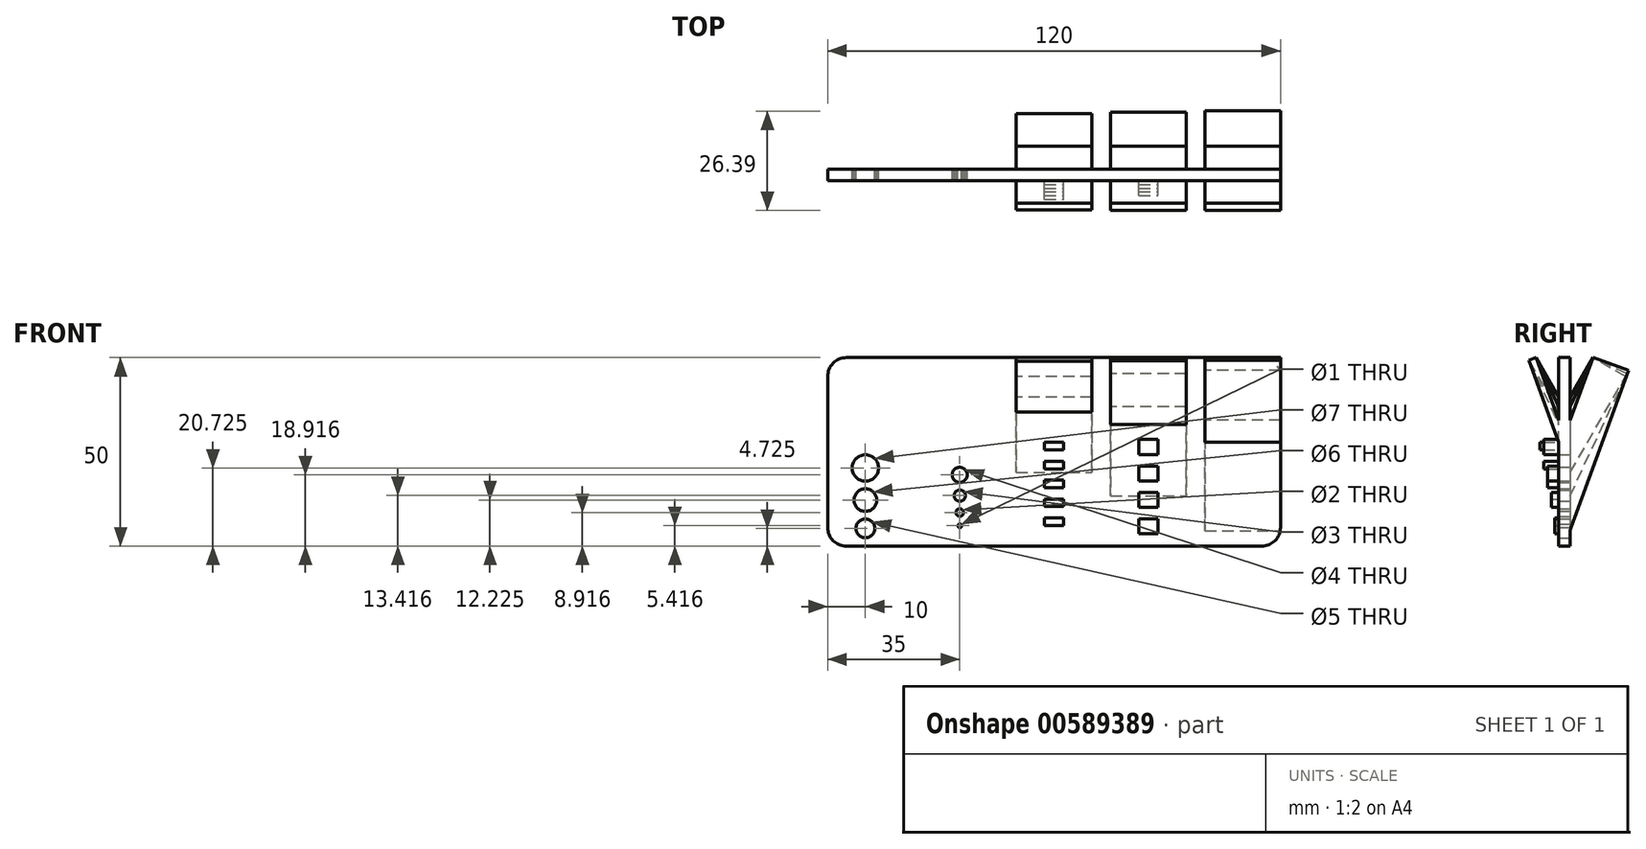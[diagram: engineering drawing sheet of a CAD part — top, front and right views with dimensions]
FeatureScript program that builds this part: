
annotation { "Feature Type Name" : "Feature", "Feature Type Description" : "" }
export const myFeature = defineFeature(function(context is Context, id is Id, definition is map)
    precondition{}
    {
        {
            var Q0;
            Q0=qCreatedBy(makeId("Top.planeOp"),FACE);
            var sketch = newSketch(context, id + "F0", { "sketchPlane" : qUnion([Q0])});
            skLineSegment(sketch, "E0", {"start": v(-60, 1.5) * mm, "end": v(-1.5, 1.5) * mm});
            skLineSegment(sketch, "E1", {"start": v(-1.5, 1.5) * mm, "end": v(-1.5, 15) * mm});
            skLineSegment(sketch, "E2", {"start": v(-1.5, 15) * mm, "end": v(1.5, 15) * mm});
            skLineSegment(sketch, "E3", {"start": v(1.5, 15) * mm, "end": v(1.5, 1.5) * mm});
            skLineSegment(sketch, "E4", {"start": v(1.5, 1.5) * mm, "end": v(60, 1.5) * mm});
            skLineSegment(sketch, "E5", {"start": v(60, 1.5) * mm, "end": v(60, -1.5) * mm});
            skLineSegment(sketch, "E6", {"start": v(60, -1.5) * mm, "end": v(1.5, -1.5) * mm});
            skLineSegment(sketch, "E7", {"start": v(1.5, -1.5) * mm, "end": v(1.5, -15) * mm});
            skLineSegment(sketch, "E8", {"start": v(1.5, -15) * mm, "end": v(-1.5, -15) * mm});
            skLineSegment(sketch, "E9", {"start": v(-1.5, -15) * mm, "end": v(-1.5, -1.5) * mm});
            skLineSegment(sketch, "E10", {"start": v(-1.5, -1.5) * mm, "end": v(-60, -1.5) * mm});
            skLineSegment(sketch, "E11", {"start": v(-60, -1.5) * mm, "end": v(-60, 1.5) * mm});
            skLineSegment(sketch, "E12", {"start": v(0, 15) * mm, "end": v(0, 0) * mm, "construction": true});
            skLineSegment(sketch, "E13", {"start": v(-60, 0) * mm, "end": v(0, 0) * mm});
            skLineSegment(sketch, "E14", {"start": v(-1.5, -1.5) * mm, "end": v(1.5, -1.5) * mm});
            skLineSegment(sketch, "E15", {"start": v(-1.5, 1.5) * mm, "end": v(1.5, 1.5) * mm});
            skLineSegment(sketch, "E16", {"start": v(1.5, 1.5) * mm, "end": v(1.5, -1.5) * mm});
            skLineSegment(sketch, "E17", {"start": v(-1.5, -1.5) * mm, "end": v(-1.5, 1.5) * mm});
            skSolve(sketch);
        }
        {
            var Q0;
            {var subQ0=sQuery(id+"F0.wireOp",EDGE,"E10");Q0=makeQuery(id+"F0.imprint","IMPRINT",FACE,{"disambiguationData":[TD([[makeQuery(id+"F0.imprint","IMPRINT",EDGE,{"derivedFrom":subQ0}),-1.0]])]});}
            var Q1;
            {var subQ0=sQuery(id+"F0.wireOp",EDGE,"E0");Q1=makeQuery(id+"F0.imprint","IMPRINT",FACE,{"disambiguationData":[TD([[makeQuery(id+"F0.imprint","IMPRINT",EDGE,{"derivedFrom":subQ0}),-1.0]])]});}
            var Q2;
            {var subQ1=sQuery(id+"F0.wireOp",EDGE,"E14");Q2=makeQuery(id+"F0.imprint","IMPRINT",FACE,{"disambiguationData":[TD([[makeQuery(id+"F0.imprint","IMPRINT",EDGE,{"derivedFrom":subQ1}),1.0]])]});}
            var Q3;
            Q3=makeQuery(id+"F0.imprint","IMPRINT",FACE,{"disambiguationData":[TD([[makeQuery(id+"F0.imprint","IMPRINT",EDGE,{"derivedFrom":sQuery(id+"F0.wireOp",EDGE,"E4")}),-1.0]])]});
            extrude(context, id + "F1", {"entities" : qUnion([Q0, Q1, Q2, Q3]), "depth" : 50 * mm, "offsetDistance" : 25 * mm});
        }
        {
            var Q0;
            Q0=qCreatedBy(makeId("Right.planeOp"),FACE);
            cPlane(context, id + "F2", {"entities" : qUnion([Q0]), "cplaneType" : CPlaneType.OFFSET, "offset" : 25 * mm, "width" : 150 * mm, "height" : 150 * mm});
        }
        {
            var Q0;
            Q0=qCreatedBy(makeId("Right.planeOp"),FACE);
            cPlane(context, id + "F3", {"entities" : qUnion([Q0]), "cplaneType" : CPlaneType.OFFSET, "offset" : 50 * mm, "width" : 150 * mm, "height" : 150 * mm});
        }
        {
            var Q0;
            Q0=qCreatedBy(id+"F3.planeOp",FACE);
            var sketch = newSketch(context, id + "F4", { "sketchPlane" : qUnion([Q0])});
            skLineSegment(sketch, "E18", {"start": v(0, 0) * mm, "end": v(16.95, 46.58) * mm});
            skLineSegment(sketch, "E19", {"start": v(16.95, 46.58) * mm, "end": v(7.56, 50) * mm});
            skLineSegment(sketch, "E20", {"start": v(7.56, 50) * mm, "end": v(0, 29.24) * mm});
            skLineSegment(sketch, "E21", {"start": v(0, 29.24) * mm, "end": v(0, 0) * mm});
            skLineSegment(sketch, "E22", {"start": v(0, 29.24) * mm, "end": v(-7.56, 50) * mm});
            skLineSegment(sketch, "E23", {"start": v(-7.56, 50) * mm, "end": v(-9.44, 49.32) * mm});
            skLineSegment(sketch, "E24", {"start": v(-9.44, 49.32) * mm, "end": v(0, 23.4) * mm});
            skLineSegment(sketch, "E25", {"start": v(0, 23.4) * mm, "end": v(0, 29.24) * mm});
            skSolve(sketch);
        }
        {
            var Q0;
            Q0=qCreatedBy(id+"F2.planeOp",FACE);
            var sketch = newSketch(context, id + "F5", { "sketchPlane" : qUnion([Q0])});
            skLineSegment(sketch, "E26", {"start": v(0, 10.13) * mm, "end": v(16.62, 45.77) * mm});
            skLineSegment(sketch, "E27", {"start": v(16.62, 45.77) * mm, "end": v(7.56, 50) * mm});
            skLineSegment(sketch, "E28", {"start": v(7.56, 50) * mm, "end": v(0, 33.8) * mm});
            skLineSegment(sketch, "E29", {"start": v(0, 33.8) * mm, "end": v(0, 10.13) * mm});
            skLineSegment(sketch, "E30", {"start": v(0, 33.8) * mm, "end": v(-7.56, 50) * mm});
            skLineSegment(sketch, "E31", {"start": v(-7.56, 50) * mm, "end": v(-9.37, 49.15) * mm});
            skLineSegment(sketch, "E32", {"start": v(-9.37, 49.15) * mm, "end": v(0, 29.06) * mm});
            skLineSegment(sketch, "E33", {"start": v(0, 29.06) * mm, "end": v(0, 33.8) * mm});
            skSolve(sketch);
        }
        {
            var Q0;
            Q0=qCreatedBy(makeId("Right.planeOp"),FACE);
            var sketch = newSketch(context, id + "F6", { "sketchPlane" : qUnion([Q0])});
            skLineSegment(sketch, "E34", {"start": v(0, 16.91) * mm, "end": v(16.22, 45) * mm});
            skLineSegment(sketch, "E35", {"start": v(16.22, 45) * mm, "end": v(7.56, 50) * mm});
            skLineSegment(sketch, "E36", {"start": v(7.56, 50) * mm, "end": v(0, 36.91) * mm});
            skLineSegment(sketch, "E37", {"start": v(0, 36.91) * mm, "end": v(0, 16.91) * mm});
            skLineSegment(sketch, "E38", {"start": v(0, 36.91) * mm, "end": v(-7.56, 50) * mm});
            skLineSegment(sketch, "E39", {"start": v(-7.56, 50) * mm, "end": v(-9.29, 49) * mm});
            skLineSegment(sketch, "E40", {"start": v(-9.29, 49) * mm, "end": v(0, 32.91) * mm});
            skLineSegment(sketch, "E41", {"start": v(0, 32.91) * mm, "end": v(0, 36.91) * mm});
            skSolve(sketch);
        }
        {
            var Q0;
            Q0=qCreatedBy(id+"F3WGKMQ0B0yvw4O_1.1.F2.planeOp",FACE);
            var sketch = newSketch(context, id + "F7", { "sketchPlane" : qUnion([Q0])});
            skLineSegment(sketch, "E42", {"start": v(0, 21.77) * mm, "end": v(-15.75, 44.26) * mm});
            skLineSegment(sketch, "E43", {"start": v(-15.75, 44.26) * mm, "end": v(-7.56, 50) * mm});
            skLineSegment(sketch, "E44", {"start": v(-7.56, 50) * mm, "end": v(0, 39.2) * mm});
            skLineSegment(sketch, "E45", {"start": v(0, 39.2) * mm, "end": v(0, 21.77) * mm});
            skLineSegment(sketch, "E46", {"start": v(0, 39.2) * mm, "end": v(7.56, 50) * mm});
            skLineSegment(sketch, "E47", {"start": v(7.56, 50) * mm, "end": v(9.2, 48.85) * mm});
            skLineSegment(sketch, "E48", {"start": v(9.2, 48.85) * mm, "end": v(0, 35.72) * mm});
            skLineSegment(sketch, "E49", {"start": v(0, 35.72) * mm, "end": v(0, 39.2) * mm});
            skSolve(sketch);
        }
        {
            var Q0;
            Q0=qCreatedBy(id+"F3WGKMQ0B0yvw4O_1.1.F3.planeOp",FACE);
            var sketch = newSketch(context, id + "F8", { "sketchPlane" : qUnion([Q0])});
            skLineSegment(sketch, "E50", {"start": v(0, 25.44) * mm, "end": v(-15.22, 43.57) * mm});
            skLineSegment(sketch, "E51", {"start": v(-15.22, 43.57) * mm, "end": v(-7.56, 50) * mm});
            skLineSegment(sketch, "E52", {"start": v(-7.56, 50) * mm, "end": v(0, 41) * mm});
            skLineSegment(sketch, "E53", {"start": v(0, 41) * mm, "end": v(0, 25.44) * mm});
            skLineSegment(sketch, "E54", {"start": v(0, 41) * mm, "end": v(7.56, 50) * mm});
            skLineSegment(sketch, "E55", {"start": v(7.56, 50) * mm, "end": v(9.09, 48.71) * mm});
            skLineSegment(sketch, "E56", {"start": v(9.09, 48.71) * mm, "end": v(0, 37.88) * mm});
            skLineSegment(sketch, "E57", {"start": v(0, 37.88) * mm, "end": v(0, 41) * mm});
            skSolve(sketch);
        }
        {
            var Q0;
            Q0 = qSketchRegion(id + "F4", true);
            var Q1;
            Q1 = qSketchRegion(id + "F5", true);
            var Q2;
            Q2 = qSketchRegion(id + "F6", true);
            var Q3;
            Q3 = qSketchRegion(id + "F7", true);
            var Q4;
            Q4 = qSketchRegion(id + "F8", true);
            extrude(context, id + "F9", {"entities" : qUnion([Q0, Q1, Q2, Q3, Q4]), "operationType" : NewBodyOperationType.ADD, "endBound" : BoundingType.SYMMETRIC, "depth" : 20 * mm, "offsetDistance" : 25 * mm});
        }
        {
            var Q0;
            Q0=makeQuery(id+"F1.opExtrude","CAP_EDGE",EDGE,{"disambiguationData":[OSD([sQuery(id+"F0.wireOp",EDGE,"E11")])],"isStart":true});
            var Q1;
            Q1=makeQuery(id+"F1.opExtrude","CAP_EDGE",EDGE,{"disambiguationData":[OSD([sQuery(id+"F0.wireOp",EDGE,"E5")])],"isStart":false});
            var Q2;
            Q2=makeQuery(id+"F1.opExtrude","CAP_EDGE",EDGE,{"disambiguationData":[OSD([sQuery(id+"F0.wireOp",EDGE,"E5")])],"isStart":true});
            var Q3;
            Q3=makeQuery(id+"F1.opExtrude","CAP_EDGE",EDGE,{"disambiguationData":[OSD([sQuery(id+"F0.wireOp",EDGE,"E11")])],"isStart":false});
            fillet(context, id + "F10", {"entities" : qUnion([Q0, Q1, Q2, Q3]), "radius" : 5 * mm, "tangentPropagation" : true, "allowEdgeOverflow" : false});
        }
        {
            var Q0;
            Q0=makeQuery(id+"F1.opExtrude","SWEPT_FACE",FACE,{"disambiguationData":[OSD([sQuery(id+"F0.wireOp",EDGE,"E0"),sQuery(id+"F0.wireOp",EDGE,"E4"),sQuery(id+"F0.wireOp",EDGE,"E15")])]});
            var sketch = newSketch(context, id + "F11", { "sketchPlane" : qUnion([Q0])});
            skCircle(sketch, "E58", {"center": v(25, 5.42) * mm, "radius": 0.5 * mm});
            skCircle(sketch, "E59", {"center": v(25, 8.92) * mm, "radius": 1 * mm});
            skCircle(sketch, "E60", {"center": v(25, 13.42) * mm, "radius": 1.5 * mm});
            skCircle(sketch, "E61", {"center": v(25, 18.92) * mm, "radius": 2 * mm});
            skCircle(sketch, "E62", {"center": v(50, 4.72) * mm, "radius": 2.5 * mm});
            skCircle(sketch, "E63", {"center": v(50, 12.22) * mm, "radius": 3 * mm});
            skCircle(sketch, "E64", {"center": v(50, 20.72) * mm, "radius": 3.5 * mm});
            skSolve(sketch);
        }
        {
            var Q0;
            Q0 = qSketchRegion(id + "F11", true);
            extrude(context, id + "F12", {"entities" : qUnion([Q0]), "operationType" : NewBodyOperationType.REMOVE, "endBound" : BoundingType.UP_TO_NEXT, "oppositeDirection" : true, "depth" : 25 * mm, "offsetDistance" : 25 * mm});
        }
        {
            var Q0;
            Q0=makeQuery(id+"F1.opExtrude","SWEPT_FACE",FACE,{"disambiguationData":[OSD([sQuery(id+"F0.wireOp",EDGE,"E6"),sQuery(id+"F0.wireOp",EDGE,"E10"),sQuery(id+"F0.wireOp",EDGE,"E14")])]});
            var sketch = newSketch(context, id + "F13", { "sketchPlane" : qUnion([Q0])});
            skLineSegment(sketch, "E65.bottom", {"start": v(-2.5, 7.5) * mm, "end": v(2.5, 7.5) * mm});
            skLineSegment(sketch, "E65.top", {"start": v(-2.5, 5.5) * mm, "end": v(2.5, 5.5) * mm});
            skLineSegment(sketch, "E65.left", {"start": v(-2.5, 7.5) * mm, "end": v(-2.5, 5.5) * mm});
            skLineSegment(sketch, "E65.right", {"start": v(2.5, 7.5) * mm, "end": v(2.5, 5.5) * mm});
            skLineSegment(sketch, "E66.1.0.0", {"start": v(-2.5, 12.5) * mm, "end": v(2.5, 12.5) * mm});
            skLineSegment(sketch, "E66.1.0.1", {"start": v(2.5, 12.5) * mm, "end": v(2.5, 10.5) * mm});
            skLineSegment(sketch, "E66.1.0.2", {"start": v(-2.5, 10.5) * mm, "end": v(2.5, 10.5) * mm});
            skLineSegment(sketch, "E66.1.0.3", {"start": v(-2.5, 12.5) * mm, "end": v(-2.5, 10.5) * mm});
            skLineSegment(sketch, "E66.2.0.0", {"start": v(-2.5, 17.5) * mm, "end": v(2.5, 17.5) * mm});
            skLineSegment(sketch, "E66.2.0.1", {"start": v(2.5, 17.5) * mm, "end": v(2.5, 15.5) * mm});
            skLineSegment(sketch, "E66.2.0.2", {"start": v(-2.5, 15.5) * mm, "end": v(2.5, 15.5) * mm});
            skLineSegment(sketch, "E66.2.0.3", {"start": v(-2.5, 17.5) * mm, "end": v(-2.5, 15.5) * mm});
            skLineSegment(sketch, "E66.3.0.0", {"start": v(-2.5, 22.5) * mm, "end": v(2.5, 22.5) * mm});
            skLineSegment(sketch, "E66.3.0.1", {"start": v(2.5, 22.5) * mm, "end": v(2.5, 20.5) * mm});
            skLineSegment(sketch, "E66.3.0.2", {"start": v(-2.5, 20.5) * mm, "end": v(2.5, 20.5) * mm});
            skLineSegment(sketch, "E66.3.0.3", {"start": v(-2.5, 22.5) * mm, "end": v(-2.5, 20.5) * mm});
            skLineSegment(sketch, "E66.4.0.0", {"start": v(-2.5, 27.5) * mm, "end": v(2.5, 27.5) * mm});
            skLineSegment(sketch, "E66.4.0.1", {"start": v(2.5, 27.5) * mm, "end": v(2.5, 25.5) * mm});
            skLineSegment(sketch, "E66.4.0.2", {"start": v(-2.5, 25.5) * mm, "end": v(2.5, 25.5) * mm});
            skLineSegment(sketch, "E66.4.0.3", {"start": v(-2.5, 27.5) * mm, "end": v(-2.5, 25.5) * mm});
            skLineSegment(sketch, "E66.direction1", {"start": v(-2.5, 7.5) * mm, "end": v(-2.5, 12.5) * mm, "construction": true});
            skSolve(sketch);
        }
        {
            var Q0;
            Q0=makeQuery(id+"F13.imprint","IMPRINT",FACE,{"disambiguationData":[TD([[makeQuery(id+"F13.imprint","IMPRINT",EDGE,{"derivedFrom":sQuery(id+"F13.wireOp",EDGE,"E65.bottom")}),1.0]])]});
            var sketch = newSketch(context, id + "F14", { "sketchPlane" : qUnion([Q0])});
            skLineSegment(sketch, "E67.bottom", {"start": v(22.5, 7.28) * mm, "end": v(27.5, 7.28) * mm});
            skLineSegment(sketch, "E67.top", {"start": v(22.5, 3.28) * mm, "end": v(27.5, 3.28) * mm});
            skLineSegment(sketch, "E67.left", {"start": v(22.5, 7.28) * mm, "end": v(22.5, 3.28) * mm});
            skLineSegment(sketch, "E67.right", {"start": v(27.5, 7.28) * mm, "end": v(27.5, 3.28) * mm});
            skLineSegment(sketch, "E68.0.1.0", {"start": v(22.5, 14.28) * mm, "end": v(27.5, 14.28) * mm});
            skLineSegment(sketch, "E68.0.1.1", {"start": v(27.5, 14.28) * mm, "end": v(27.5, 10.28) * mm});
            skLineSegment(sketch, "E68.0.1.2", {"start": v(22.5, 14.28) * mm, "end": v(22.5, 10.28) * mm});
            skLineSegment(sketch, "E68.0.1.3", {"start": v(22.5, 10.28) * mm, "end": v(27.5, 10.28) * mm});
            skLineSegment(sketch, "E68.0.2.0", {"start": v(22.5, 21.28) * mm, "end": v(27.5, 21.28) * mm});
            skLineSegment(sketch, "E68.0.2.1", {"start": v(27.5, 21.28) * mm, "end": v(27.5, 17.28) * mm});
            skLineSegment(sketch, "E68.0.2.2", {"start": v(22.5, 21.28) * mm, "end": v(22.5, 17.28) * mm});
            skLineSegment(sketch, "E68.0.2.3", {"start": v(22.5, 17.28) * mm, "end": v(27.5, 17.28) * mm});
            skLineSegment(sketch, "E68.0.3.0", {"start": v(22.5, 28.28) * mm, "end": v(27.5, 28.28) * mm});
            skLineSegment(sketch, "E68.0.3.1", {"start": v(27.5, 28.28) * mm, "end": v(27.5, 24.28) * mm});
            skLineSegment(sketch, "E68.0.3.2", {"start": v(22.5, 28.28) * mm, "end": v(22.5, 24.28) * mm});
            skLineSegment(sketch, "E68.0.3.3", {"start": v(22.5, 24.28) * mm, "end": v(27.5, 24.28) * mm});
            skLineSegment(sketch, "E68.direction1", {"start": v(22.5, 3.28) * mm, "end": v(47.5, 3.28) * mm, "construction": true});
            skLineSegment(sketch, "E68.direction2", {"start": v(22.5, 3.28) * mm, "end": v(22.5, 10.28) * mm, "construction": true});
            skSolve(sketch);
        }
        {
            var Q0;
            Q0=makeQuery(id+"F13.imprint","IMPRINT",FACE,{"disambiguationData":[TD([[makeQuery(id+"F13.imprint","IMPRINT",EDGE,{"derivedFrom":sQuery(id+"F13.wireOp",EDGE,"E65.bottom")}),-1.0]])]});
            var Q1;
            Q1=makeQuery(id+"F14.imprint","IMPRINT",FACE,{"disambiguationData":[TD([[makeQuery(id+"F14.imprint","IMPRINT",EDGE,{"derivedFrom":sQuery(id+"F14.wireOp",EDGE,"E67.bottom")}),-1.0]])]});
            extrude(context, id + "F15", {"entities" : qUnion([Q0, Q1]), "operationType" : NewBodyOperationType.ADD, "depth" : 1 * mm, "offsetDistance" : 25 * mm});
        }
        {
            var Q0;
            Q0=makeQuery(id+"F13.imprint","IMPRINT",FACE,{"disambiguationData":[TD([[makeQuery(id+"F13.imprint","IMPRINT",EDGE,{"derivedFrom":sQuery(id+"F13.wireOp",EDGE,"E66.1.0.0")}),-1.0]])]});
            var Q1;
            Q1=makeQuery(id+"F14.imprint","IMPRINT",FACE,{"disambiguationData":[TD([[makeQuery(id+"F14.imprint","IMPRINT",EDGE,{"derivedFrom":sQuery(id+"F14.wireOp",EDGE,"E68.0.1.0")}),-1.0]])]});
            extrude(context, id + "F16", {"entities" : qUnion([Q0, Q1]), "operationType" : NewBodyOperationType.ADD, "depth" : 2 * mm, "offsetDistance" : 25 * mm});
        }
        {
            var Q0;
            Q0=makeQuery(id+"F13.imprint","IMPRINT",FACE,{"disambiguationData":[TD([[makeQuery(id+"F13.imprint","IMPRINT",EDGE,{"derivedFrom":sQuery(id+"F13.wireOp",EDGE,"E66.2.0.0")}),-1.0]])]});
            var Q1;
            Q1=makeQuery(id+"F14.imprint","IMPRINT",FACE,{"disambiguationData":[TD([[makeQuery(id+"F14.imprint","IMPRINT",EDGE,{"derivedFrom":sQuery(id+"F14.wireOp",EDGE,"E68.0.2.0")}),-1.0]])]});
            extrude(context, id + "F17", {"entities" : qUnion([Q0, Q1]), "operationType" : NewBodyOperationType.ADD, "depth" : 3 * mm, "offsetDistance" : 25 * mm});
        }
        {
            var Q0;
            Q0=makeQuery(id+"F13.imprint","IMPRINT",FACE,{"disambiguationData":[TD([[makeQuery(id+"F13.imprint","IMPRINT",EDGE,{"derivedFrom":sQuery(id+"F13.wireOp",EDGE,"E66.3.0.0")}),-1.0]])]});
            var Q1;
            Q1=makeQuery(id+"F14.imprint","IMPRINT",FACE,{"disambiguationData":[TD([[makeQuery(id+"F14.imprint","IMPRINT",EDGE,{"derivedFrom":sQuery(id+"F14.wireOp",EDGE,"E68.0.3.0")}),-1.0]])]});
            extrude(context, id + "F18", {"entities" : qUnion([Q0, Q1]), "operationType" : NewBodyOperationType.ADD, "depth" : 4 * mm, "offsetDistance" : 25 * mm});
        }
        {
            var Q0;
            Q0=makeQuery(id+"F13.imprint","IMPRINT",FACE,{"disambiguationData":[TD([[makeQuery(id+"F13.imprint","IMPRINT",EDGE,{"derivedFrom":sQuery(id+"F13.wireOp",EDGE,"E66.4.0.0")}),-1.0]])]});
            extrude(context, id + "F19", {"entities" : qUnion([Q0]), "operationType" : NewBodyOperationType.ADD, "depth" : 5 * mm, "offsetDistance" : 25 * mm});
        }
    });
